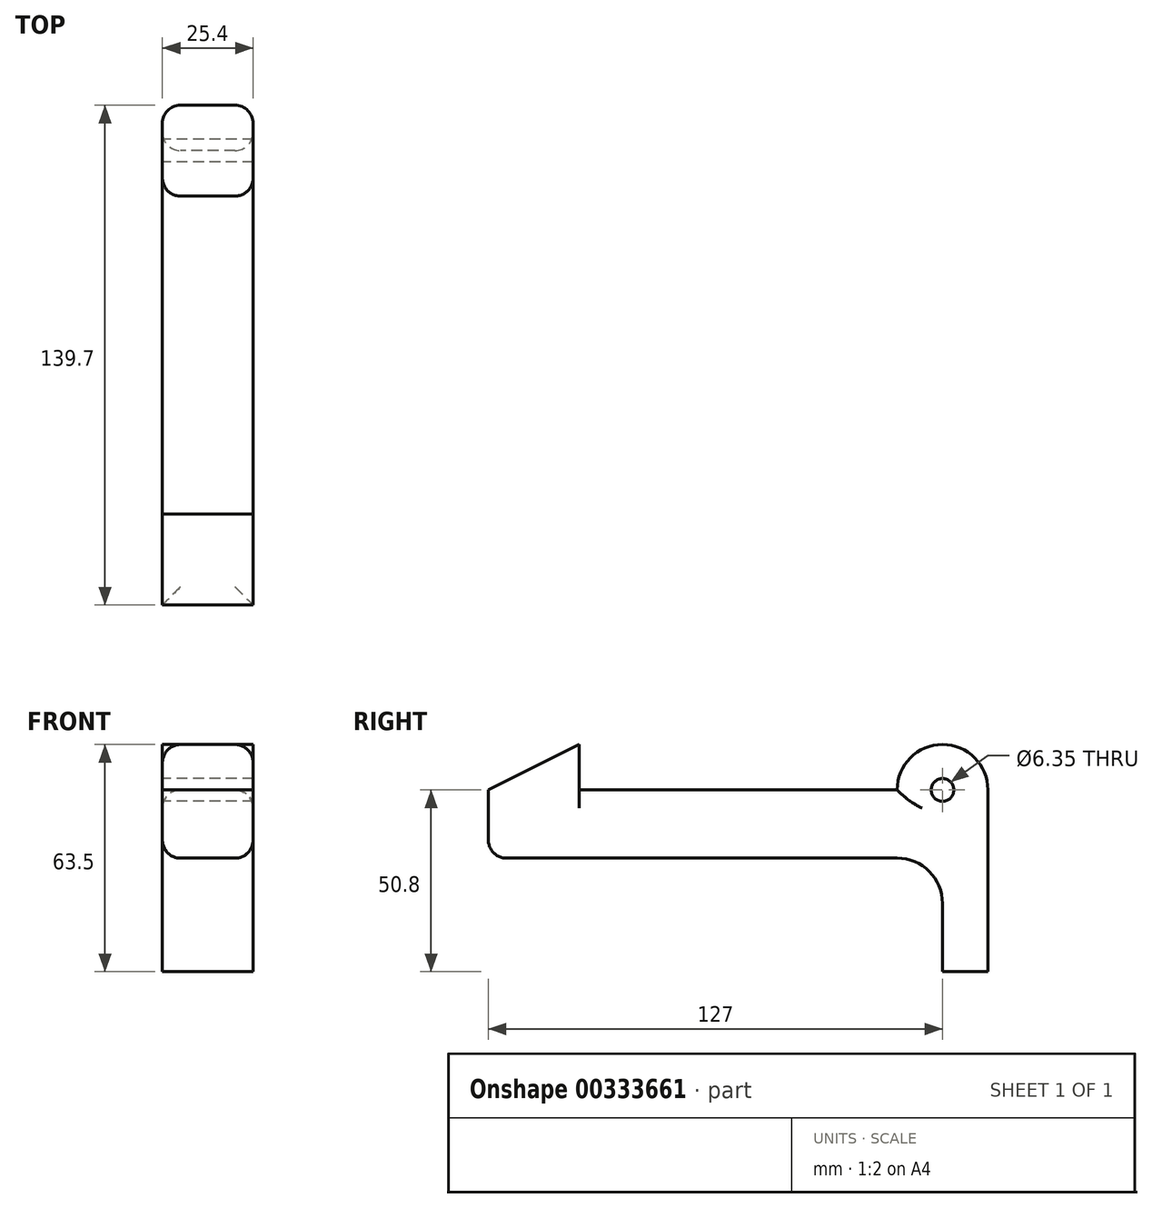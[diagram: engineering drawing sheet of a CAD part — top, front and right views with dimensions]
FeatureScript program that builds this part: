
annotation { "Feature Type Name" : "Feature", "Feature Type Description" : "" }
export const myFeature = defineFeature(function(context is Context, id is Id, definition is map)
    precondition{}
    {
        {
            var Q0;
            Q0=qCreatedBy(makeId("Right.planeOp"),FACE);
            var sketch = newSketch(context, id + "F0", { "sketchPlane" : qUnion([Q0])});
            skLineSegment(sketch, "E0.bottom", {"start": v(0, 0) * mm, "end": v(-114.3, 0) * mm});
            skLineSegment(sketch, "E0.top", {"start": v(0, 19.05) * mm, "end": v(-88.9, 19.05) * mm});
            skLineSegment(sketch, "E0.left", {"start": v(0, 0) * mm, "end": v(0, 19.05) * mm});
            skLineSegment(sketch, "E0.right", {"start": v(-114.3, 0) * mm, "end": v(-114.3, 19.05) * mm});
            skArc(sketch, "E1", {"start": v(25.4, 19.05) * mm, "mid": v(12.7, 31.75) * mm, "end": v(0, 19.05) * mm});
            skPoint(sketch, "E2", {"position": v(25.4, 19.05) * mm});
            skLineSegment(sketch, "E3.top", {"start": v(12.7, -31.75) * mm, "end": v(25.4, -31.75) * mm});
            skLineSegment(sketch, "E3.left", {"start": v(12.7, -12.7) * mm, "end": v(12.7, -31.75) * mm});
            skLineSegment(sketch, "E3.right", {"start": v(25.4, 19.05) * mm, "end": v(25.4, -31.75) * mm});
            skArc(sketch, "E4", {"start": v(12.7, -12.7) * mm, "mid": v(8.98, -3.72) * mm, "end": v(0, 0) * mm});
            skPoint(sketch, "E5", {"position": v(12.7, -12.7) * mm});
            skPoint(sketch, "E6.orphan", {"position": v(12.7, 6.35) * mm});
            skCircle(sketch, "E7", {"center": v(12.7, 19.05) * mm, "radius": 3.18 * mm});
            skLineSegment(sketch, "E8.right", {"start": v(-88.9, 19.05) * mm, "end": v(-88.9, 31.75) * mm});
            skLineSegment(sketch, "E9", {"start": v(-88.9, 31.75) * mm, "end": v(-114.3, 19.05) * mm});
            skSolve(sketch);
        }
        {
            var Q0;
            Q0 = qSketchRegion(id + "F0", true);
            extrude(context, id + "F1", {"entities" : qUnion([Q0]), "depth" : 25.4 * mm});
        }
        {
            var Q0;
            Q0=makeQuery(id+"F1.opExtrude","CAP_EDGE",EDGE,{"disambiguationData":[OSD([sQuery(id+"F0.wireOp",EDGE,"E0.bottom")])],"isStart":false});
            var Q1;
            Q1=makeQuery(id+"F1.opExtrude","CAP_EDGE",EDGE,{"disambiguationData":[OSD([sQuery(id+"F0.wireOp",EDGE,"E0.bottom")])],"isStart":true});
            var Q2;
            Q2=makeQuery(id+"F1.opExtrude","CAP_EDGE",EDGE,{"disambiguationData":[OSD([sQuery(id+"F0.wireOp",EDGE,"E3.right")])],"isStart":false});
            var Q3;
            Q3=makeQuery(id+"F1.opExtrude","CAP_EDGE",EDGE,{"disambiguationData":[OSD([sQuery(id+"F0.wireOp",EDGE,"E3.right")])],"isStart":true});
            var Q4;
            Q4=makeQuery(id+"F1.opExtrude","CAP_EDGE",EDGE,{"disambiguationData":[OSD([sQuery(id+"F0.wireOp",EDGE,"E0.top")])],"isStart":true});
            var Q5;
            Q5=makeQuery(id+"F1.opExtrude","CAP_EDGE",EDGE,{"disambiguationData":[OSD([sQuery(id+"F0.wireOp",EDGE,"E0.top")])],"isStart":false});
            var Q6;
            Q6=makeQuery(id+"F1.opExtrude","SWEPT_EDGE",EDGE,{"disambiguationData":[OSD([sQuery(id+"F0.wireOp",EDGE,"E0.bottom"),sQuery(id+"F0.wireOp",EDGE,"E0.right")])]});
            fillet(context, id + "F2", {"entities" : qUnion([Q0, Q1, Q2, Q3, Q4, Q5, Q6]), "radius" : 5.08 * mm, "tangentPropagation" : true, "allowEdgeOverflow" : false});
        }
    });
